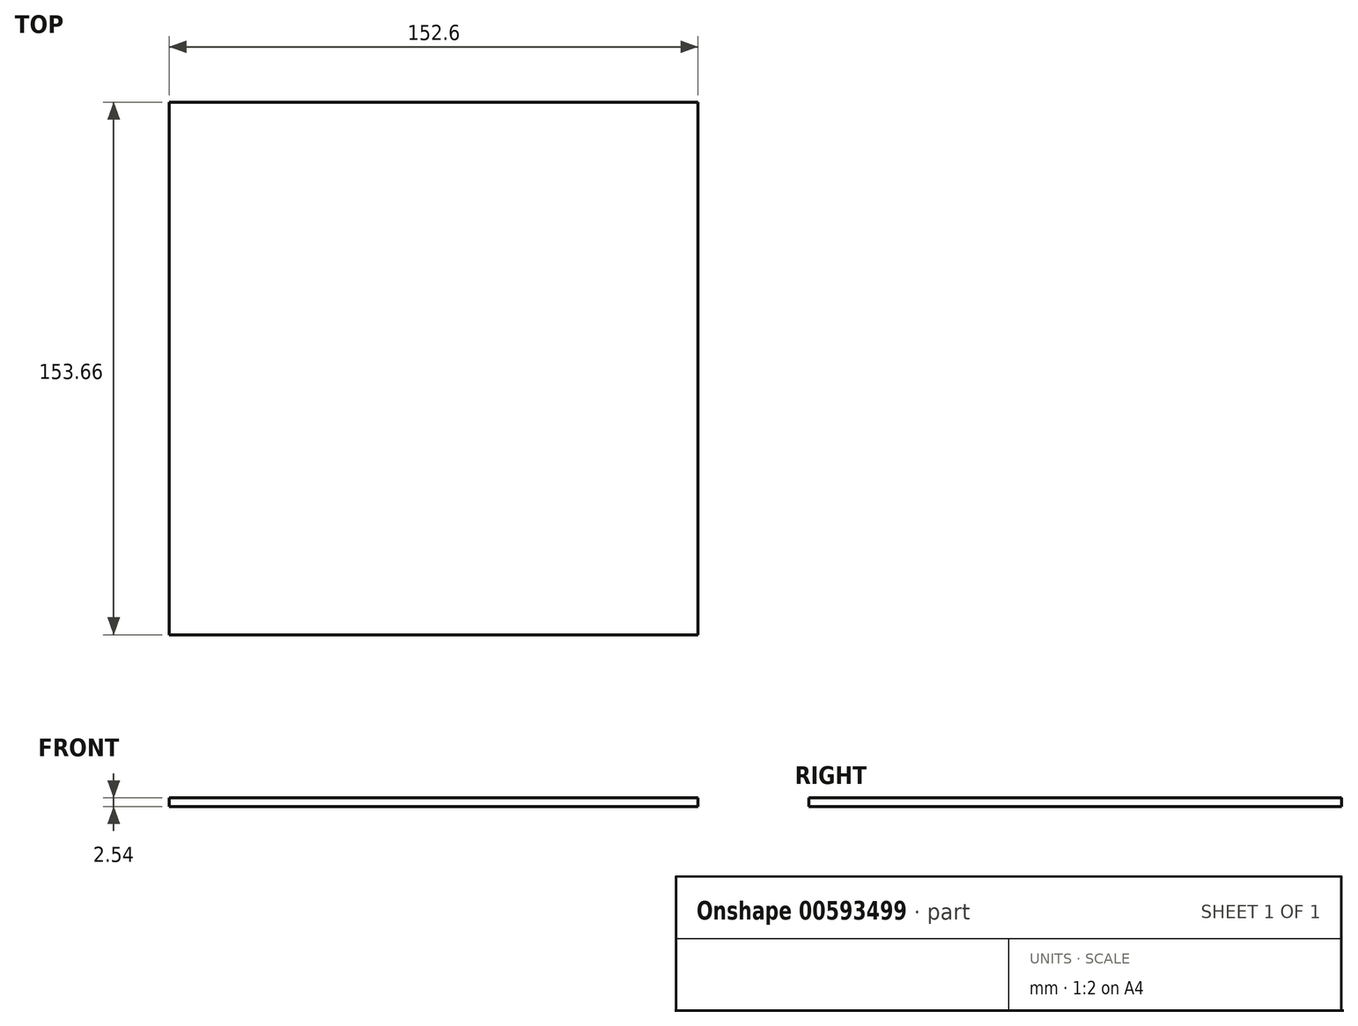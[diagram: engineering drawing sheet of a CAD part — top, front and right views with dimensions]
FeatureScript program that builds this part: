
annotation { "Feature Type Name" : "Feature", "Feature Type Description" : "" }
export const myFeature = defineFeature(function(context is Context, id is Id, definition is map)
    precondition{}
    {
        {
            var Q0;
            Q0=qCreatedBy(makeId("Top.planeOp"),FACE);
            var sketch = newSketch(context, id + "F0", { "sketchPlane" : qUnion([Q0])});
            skLineSegment(sketch, "E0.bottom", {"start": v(-77.23, 77.5) * mm, "end": v(75.37, 77.5) * mm});
            skLineSegment(sketch, "E0.top", {"start": v(-77.23, -76.17) * mm, "end": v(75.37, -76.17) * mm});
            skLineSegment(sketch, "E0.left", {"start": v(-77.23, 77.5) * mm, "end": v(-77.23, -76.17) * mm});
            skLineSegment(sketch, "E0.right", {"start": v(75.37, 77.5) * mm, "end": v(75.37, -76.17) * mm});
            skSolve(sketch);
        }
        {
            var Q0;
            Q0 = qSketchRegion(id + "F0", true);
            extrude(context, id + "F1", {"entities" : qUnion([Q0]), "depth" : 2.54 * mm, "offsetDistance" : 25.4 * mm});
        }
    });
